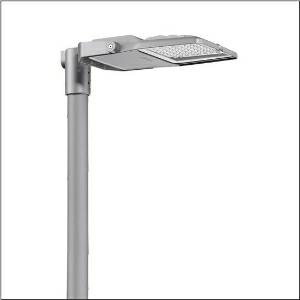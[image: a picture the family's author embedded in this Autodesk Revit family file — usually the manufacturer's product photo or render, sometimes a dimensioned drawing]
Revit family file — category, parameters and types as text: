
# Revit family: floodlight_fl_21_iq_mini___pl52_5xa7771d4d3a_bc98
name_source: partatom
category: Lighting Fixtures
units: mm (PartAtom-declared; Revit-internal decimal feet)

## family parameters
Cut with Voids When Loaded = No
Host = Face
Light Source = No
Part Type = Normal
Room Calculation Point = No
Round Connector Dimension = Use Diameter
Shared = No

## types (1)
- --- (1 x LED, 18610 lm, 143 W, 4000K)
    Apparent Load = 143 VA
    CIE Flux Codes = 26 60 98 100 100
    Color Rendering = 70
    Color Temperature = 4000K
    Default Elevation = 1800 mm
    Description = Floodlight FL 21 iQ mini, floodlight, primary light control with lens, of PMMA, primary optical cover: protective disc, of toughened safety glass, transparent, light distribution: PL52, light emission: direct distribution, installation type: surface-mounted, LED, High Power LED, rated luminous flux: 18.610lm, luminous efficacy: 130lm/W, light colour: 740, colour temperature: 4000K, control gear: iQ Comfort/DALI, control: Auto-Match, Temp-Guard, Lumen-Switch, Night-Set, Smart-Wire, Light-Fading, Desk-Remote (wireless, voltage-free reading and setting of iQ features in the workshop via application-optimized NFC function/RFID function), optimised constant luminous flux control (CLO 2.0), with terminal, 6-pole, mains connection: 220..240V, AC, 50/60Hz, start of lifetime: 143W, end of service life: 152W, reduction: 61W, luminaire housing, of diecast aluminium, powder-coated, Siteco® metallic grey (DB 702S), corrosivity category C5 mid according to DIN EN ISO 12944, suitable for swimming pools, chlorine-resistant, sealing non-destructively replaceable, please order mast flange separately, mast bracket, of steel, galvanised, powder-coated, Siteco® metallic grey (DB 702S), protection rating (complete): IP66, insulation class (complete): insulation class II (safety insulation), certification: CE, ENEC, VDE, protection symbol: D, impact resistance: IK08, permissible operating ambient temperature: -40..+40°C, permissible operating ambient temperature for outdoor applications: -40..+50°C, standard: DIN EN 12944, LABS conformity tested according to VDMA 24364:2018-05, packaging unit: 1 piece

Light Distribution: PL52
    Height = 70 mm
    Lamp = 1 x LED
    Lamp Light Flux = 18610 lm
    Lamp Power = 143 W
    Lamp count = 1
    Length = 485 mm
    Luminous efficacy = 130 lm/W
    Manufacturer = Siteco
    ModVariant = No
    Model = 5XA7771D4D3A
    Number of Poles = 1
    OnlyDefault = Yes
    Power Factor = 1
    Product Name = Floodlight FL 21 iQ mini | PL52
    Product group = floodlight | pylon annexe
    ProductGroupID = 6201
    Protection Class = Protection class II
    Protection Degree = IP 66
    RLX_Detail_Level = 1
    RLX_Emergency_Light_Flux = 0 lm
    RLX_Emergency_Type = 0
    RLX_Emergency_Type_DB = No
    RlxData = <blob elided: 101805 chars, md5=2f65bc1a>
    Socket = socket
    Standby Power = 0 W
    System Light Flux = 18610 lm
    System Power = 143 W
    Type Comments = factory setting: luminous flux: 100 % | dim-lin: 254 | 730 mA
    Type Image = l_1007125.jpg
    URL = http://relux.com
    VarID = @adj_185321
    Voltage = 0 V
    Weight = 0.00 kg
    Width = 337 mm

## geometry (parser evidence)
native form markers: Blend x4, Sweep x11
no freeform markers — native parametric forms only
